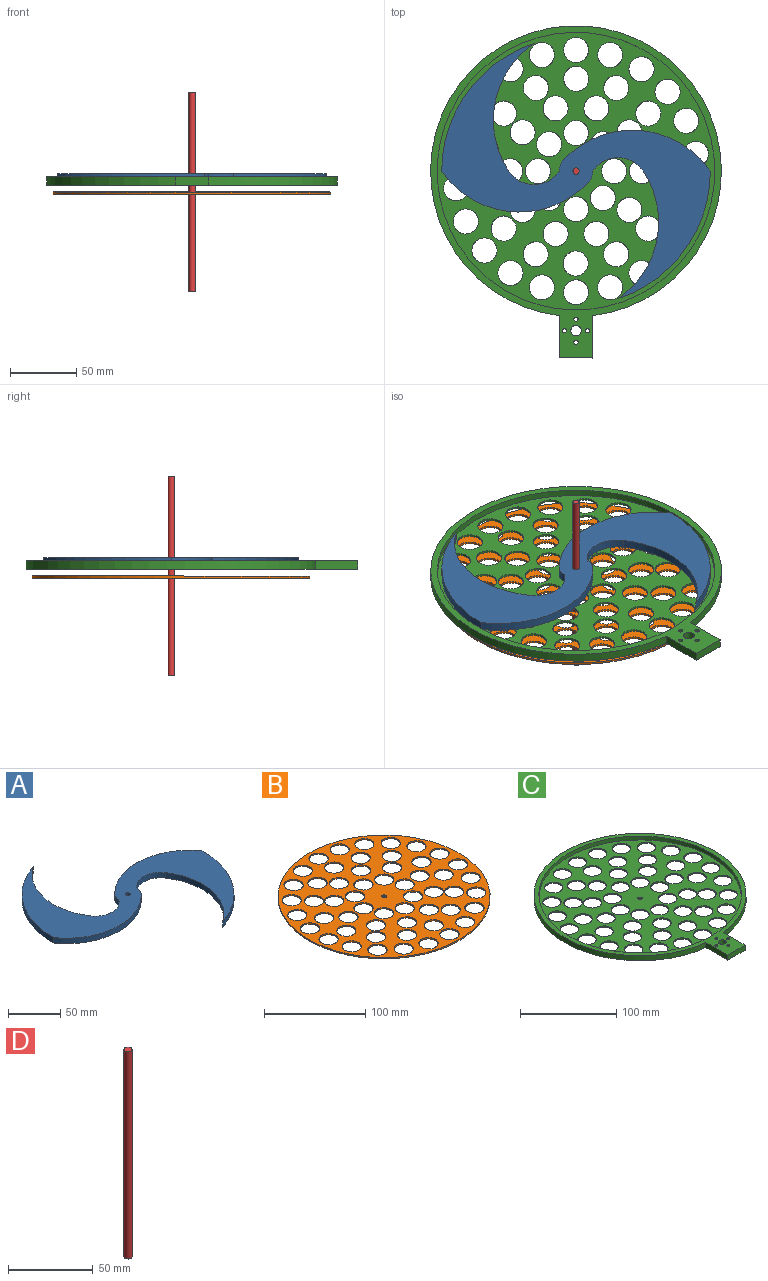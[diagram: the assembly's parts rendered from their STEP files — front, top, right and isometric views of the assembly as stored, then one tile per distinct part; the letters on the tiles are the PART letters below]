
ASSEMBLY  parts=4 mates=3
PART A: 13 faces, bbox 203.2x193x6.4 mm
  f0: cylinder r=22.9mm len=38.1mm, axis (0,0,-1), area 285.8mm2, adj f1,f10,f11,f12
  f1: cylinder r=69.74mm len=96.52mm, axis (0,0,-1), area 693.4mm2, adj f0,f2,f11,f12
  f2: cylinder r=101.6mm len=96.52mm, axis (0,0,-1), area 808.4mm2, adj f1,f3,f11,f12
  f3: cylinder r=71.61mm len=110.79mm, axis (0,0,-1), area 807.8mm2, adj f2,f4,f11,f12
  f4: cylinder r=12.7mm len=8.76mm, axis (0,0,-1), area 61.4mm2, adj f3,f5,f11,f12
  f5: cylinder r=22.9mm len=38.1mm, axis (0,0,-1), area 285.8mm2, adj f4,f6,f11,f12
  f6: cylinder r=69.74mm len=96.52mm, axis (0,0,-1), area 693.4mm2, adj f5,f7,f11,f12
  f7: cylinder r=101.6mm len=96.52mm, axis (0,0,-1), area 808.4mm2, adj f6,f8,f11,f12
  f8: cylinder r=71.6mm len=110.79mm, axis (0,0,-1), area 807.9mm2, adj f7,f10,f11,f12
  f9: cylinder r=2.38mm len=6.35mm, axis (0,0,-1), area 95mm2, adj f11,f12
  f10: cylinder r=12.7mm len=8.76mm, axis (0,0,-1), area 61.4mm2, adj f0,f8,f11,f12
  f11: plane 203.2x193.04mm, normal (0,0,1), area 9819.9mm2, adj f0,f1,f2,f3,f4,f5,f6,f7
  f12: plane 203.2x193.04mm, normal (0,0,-1), area 9819.9mm2, adj f0,f1,f2,f3,f4,f5,f6,f7
PART B: 58 faces, bbox 210x210x1.5 mm
  f0: cylinder r=9.53mm len=19.05mm, axis (0,0,-1), area 90.9mm2, adj f56,f57
  f1: cylinder r=9.53mm len=19.05mm, axis (0,0,-1), area 90.9mm2, adj f56,f57
  f2: cylinder r=9.53mm len=19.05mm, axis (0,0,-1), area 90.9mm2, adj f56,f57
  f3: cylinder r=9.53mm len=19.05mm, axis (0,0,-1), area 90.9mm2, adj f56,f57
  f4: cylinder r=9.53mm len=19.05mm, axis (0,0,-1), area 90.9mm2, adj f56,f57
  f5: cylinder r=9.53mm len=19.05mm, axis (0,0,-1), area 90.9mm2, adj f56,f57
  f6: cylinder r=9.53mm len=19.05mm, axis (0,0,-1), area 90.9mm2, adj f56,f57
  f7: cylinder r=9.53mm len=19.05mm, axis (0,0,-1), area 90.9mm2, adj f56,f57
  f8: cylinder r=9.53mm len=19.05mm, axis (0,0,-1), area 90.9mm2, adj f56,f57
  f9: cylinder r=9.53mm len=19.05mm, axis (0,0,-1), area 90.9mm2, adj f56,f57
  f10: cylinder r=9.53mm len=19.05mm, axis (0,0,-1), area 90.9mm2, adj f56,f57
  f11: cylinder r=9.53mm len=19.05mm, axis (0,0,-1), area 90.9mm2, adj f56,f57
  f12: cylinder r=9.53mm len=19.05mm, axis (0,0,-1), area 90.9mm2, adj f56,f57
  f13: cylinder r=9.53mm len=19.05mm, axis (0,0,-1), area 90.9mm2, adj f56,f57
  f14: cylinder r=9.53mm len=19.05mm, axis (0,0,-1), area 90.9mm2, adj f56,f57
  f15: cylinder r=9.53mm len=19.05mm, axis (0,0,-1), area 90.9mm2, adj f56,f57
  f16: cylinder r=9.53mm len=19.05mm, axis (0,0,-1), area 90.9mm2, adj f56,f57
  f17: cylinder r=9.53mm len=19.05mm, axis (0,0,-1), area 90.9mm2, adj f56,f57
  f18: cylinder r=9.53mm len=19.05mm, axis (0,0,-1), area 90.9mm2, adj f56,f57
  f19: cylinder r=9.53mm len=19.05mm, axis (0,0,-1), area 90.9mm2, adj f56,f57
  f20: cylinder r=9.53mm len=19.05mm, axis (0,0,-1), area 90.9mm2, adj f56,f57
  f21: cylinder r=9.53mm len=19.05mm, axis (0,0,-1), area 90.9mm2, adj f56,f57
  f22: cylinder r=9.53mm len=19.05mm, axis (0,0,-1), area 90.9mm2, adj f56,f57
  f23: cylinder r=9.53mm len=19.05mm, axis (0,0,-1), area 90.9mm2, adj f56,f57
  f24: cylinder r=9.53mm len=19.05mm, axis (0,0,-1), area 90.9mm2, adj f56,f57
  f25: cylinder r=9.53mm len=19.05mm, axis (0,0,-1), area 90.9mm2, adj f56,f57
  f26: cylinder r=9.53mm len=19.05mm, axis (0,0,-1), area 90.9mm2, adj f56,f57
  f27: cylinder r=9.53mm len=19.05mm, axis (0,0,-1), area 90.9mm2, adj f56,f57
  f28: cylinder r=9.53mm len=19.05mm, axis (0,0,-1), area 90.9mm2, adj f56,f57
  f29: cylinder r=9.53mm len=19.05mm, axis (0,0,-1), area 90.9mm2, adj f56,f57
  f30: cylinder r=9.53mm len=19.05mm, axis (0,0,-1), area 90.9mm2, adj f56,f57
  f31: cylinder r=9.53mm len=19.05mm, axis (0,0,-1), area 90.9mm2, adj f56,f57
  f32: cylinder r=9.53mm len=19.05mm, axis (0,0,-1), area 90.9mm2, adj f56,f57
  f33: cylinder r=9.53mm len=19.05mm, axis (0,0,-1), area 90.9mm2, adj f56,f57
  f34: cylinder r=2.38mm len=4.76mm, axis (0,0,-1), area 22.7mm2, adj f56,f57
  f35: cylinder r=9.53mm len=19.05mm, axis (0,0,-1), area 90.9mm2, adj f56,f57
  f36: cylinder r=9.53mm len=19.05mm, axis (0,0,-1), area 90.9mm2, adj f56,f57
  f37: cylinder r=9.53mm len=19.05mm, axis (0,0,-1), area 90.9mm2, adj f56,f57
  f38: cylinder r=9.53mm len=19.05mm, axis (0,0,-1), area 90.9mm2, adj f56,f57
  f39: cylinder r=9.53mm len=19.05mm, axis (0,0,-1), area 90.9mm2, adj f56,f57
  f40: cylinder r=9.53mm len=19.05mm, axis (0,0,-1), area 90.9mm2, adj f56,f57
  f41: cylinder r=9.53mm len=19.05mm, axis (0,0,-1), area 90.9mm2, adj f56,f57
  f42: cylinder r=9.53mm len=19.05mm, axis (0,0,-1), area 90.9mm2, adj f56,f57
  f43: cylinder r=9.53mm len=19.05mm, axis (0,0,-1), area 90.9mm2, adj f56,f57
  f44: cylinder r=9.53mm len=19.05mm, axis (0,0,-1), area 90.9mm2, adj f56,f57
  f45: cylinder r=9.53mm len=19.05mm, axis (0,0,-1), area 90.9mm2, adj f56,f57
  f46: cylinder r=9.53mm len=19.05mm, axis (0,0,-1), area 90.9mm2, adj f56,f57
  f47: cylinder r=9.53mm len=19.05mm, axis (0,0,-1), area 90.9mm2, adj f56,f57
  f48: cylinder r=9.53mm len=19.05mm, axis (0,0,-1), area 90.9mm2, adj f56,f57
  f49: cylinder r=9.53mm len=19.05mm, axis (0,0,-1), area 90.9mm2, adj f56,f57
  f50: cylinder r=9.53mm len=19.05mm, axis (0,0,-1), area 90.9mm2, adj f56,f57
  f51: cylinder r=9.53mm len=19.05mm, axis (0,0,-1), area 90.9mm2, adj f56,f57
  f52: cylinder r=9.53mm len=19.05mm, axis (0,0,-1), area 90.9mm2, adj f56,f57
  f53: cylinder r=9.53mm len=19.05mm, axis (0,0,-1), area 90.9mm2, adj f56,f57
  f54: cylinder r=9.53mm len=19.05mm, axis (0,0,-1), area 90.9mm2, adj f56,f57
  f55: cylinder r=105mm len=210mm, axis (0,0,-1), area 1002.1mm2, adj f56,f57
  f56: plane 210x210mm, normal (0,0,1), area 19227mm2, adj f0,f1,f2,f3,f4,f5,f6,f7
  f57: plane 210x210mm, normal (0,0,-1), area 19227mm2, adj f0,f1,f2,f3,f4,f5,f6,f7
PART C: 68 faces, bbox 220x251.3x6.4 mm
  f0: cylinder r=9.53mm len=19.05mm, axis (0,0,-1), area 90.9mm2, adj f55,f56
  f1: cylinder r=9.53mm len=19.05mm, axis (0,0,-1), area 90.9mm2, adj f55,f56
  f2: cylinder r=2.38mm len=4.76mm, axis (0,0,-1), area 22.7mm2, adj f55,f56
  f3: cylinder r=9.53mm len=19.05mm, axis (0,0,-1), area 90.9mm2, adj f55,f56
  f4: cylinder r=9.53mm len=19.05mm, axis (0,0,-1), area 90.9mm2, adj f55,f56
  f5: cylinder r=9.53mm len=19.05mm, axis (0,0,-1), area 90.9mm2, adj f55,f56
  f6: cylinder r=9.53mm len=19.05mm, axis (0,0,-1), area 90.9mm2, adj f55,f56
  f7: cylinder r=9.53mm len=19.05mm, axis (0,0,-1), area 90.9mm2, adj f55,f56
  f8: cylinder r=9.53mm len=19.05mm, axis (0,0,-1), area 90.9mm2, adj f55,f56
  f9: cylinder r=9.53mm len=19.05mm, axis (0,0,-1), area 90.9mm2, adj f55,f56
  f10: cylinder r=9.53mm len=19.05mm, axis (0,0,-1), area 90.9mm2, adj f55,f56
  f11: cylinder r=9.53mm len=19.05mm, axis (0,0,-1), area 90.9mm2, adj f55,f56
  f12: cylinder r=9.53mm len=19.05mm, axis (0,0,-1), area 90.9mm2, adj f55,f56
  f13: cylinder r=9.53mm len=19.05mm, axis (0,0,-1), area 90.9mm2, adj f55,f56
  f14: cylinder r=9.53mm len=19.05mm, axis (0,0,-1), area 90.9mm2, adj f55,f56
  f15: cylinder r=9.53mm len=19.05mm, axis (0,0,-1), area 90.9mm2, adj f55,f56
  f16: cylinder r=9.53mm len=19.05mm, axis (0,0,-1), area 90.9mm2, adj f55,f56
  f17: cylinder r=9.53mm len=19.05mm, axis (0,0,-1), area 90.9mm2, adj f55,f56
  f18: cylinder r=9.53mm len=19.05mm, axis (0,0,-1), area 90.9mm2, adj f55,f56
  f19: cylinder r=9.53mm len=19.05mm, axis (0,0,-1), area 90.9mm2, adj f55,f56
  f20: cylinder r=9.53mm len=19.05mm, axis (0,0,-1), area 90.9mm2, adj f55,f56
  f21: cylinder r=9.53mm len=19.05mm, axis (0,0,-1), area 90.9mm2, adj f55,f56
  f22: cylinder r=9.53mm len=19.05mm, axis (0,0,-1), area 90.9mm2, adj f55,f56
  f23: cylinder r=9.53mm len=19.05mm, axis (0,0,-1), area 90.9mm2, adj f55,f56
  f24: cylinder r=9.53mm len=19.05mm, axis (0,0,-1), area 90.9mm2, adj f55,f56
  f25: cylinder r=9.53mm len=19.05mm, axis (0,0,-1), area 90.9mm2, adj f55,f56
  f26: cylinder r=9.53mm len=19.05mm, axis (0,0,-1), area 90.9mm2, adj f55,f56
  f27: cylinder r=9.53mm len=19.05mm, axis (0,0,-1), area 90.9mm2, adj f55,f56
  f28: cylinder r=9.53mm len=19.05mm, axis (0,0,-1), area 90.9mm2, adj f55,f56
  f29: cylinder r=9.53mm len=19.05mm, axis (0,0,-1), area 90.9mm2, adj f55,f56
  f30: cylinder r=9.53mm len=19.05mm, axis (0,0,-1), area 90.9mm2, adj f55,f56
  f31: cylinder r=9.53mm len=19.05mm, axis (0,0,-1), area 90.9mm2, adj f55,f56
  f32: cylinder r=9.53mm len=19.05mm, axis (0,0,-1), area 90.9mm2, adj f55,f56
  f33: cylinder r=9.53mm len=19.05mm, axis (0,0,-1), area 90.9mm2, adj f55,f56
  f34: cylinder r=9.53mm len=19.05mm, axis (0,0,-1), area 90.9mm2, adj f55,f56
  f35: cylinder r=9.53mm len=19.05mm, axis (0,0,-1), area 90.9mm2, adj f55,f56
  f36: cylinder r=9.53mm len=19.05mm, axis (0,0,-1), area 90.9mm2, adj f55,f56
  f37: cylinder r=9.53mm len=19.05mm, axis (0,0,-1), area 90.9mm2, adj f55,f56
  f38: cylinder r=9.53mm len=19.05mm, axis (0,0,-1), area 90.9mm2, adj f55,f56
  f39: cylinder r=9.53mm len=19.05mm, axis (0,0,-1), area 90.9mm2, adj f55,f56
  f40: cylinder r=9.53mm len=19.05mm, axis (0,0,-1), area 90.9mm2, adj f55,f56
  f41: cylinder r=9.53mm len=19.05mm, axis (0,0,-1), area 90.9mm2, adj f55,f56
  f42: cylinder r=9.53mm len=19.05mm, axis (0,0,-1), area 90.9mm2, adj f55,f56
  f43: cylinder r=9.53mm len=19.05mm, axis (0,0,-1), area 90.9mm2, adj f55,f56
  f44: cylinder r=9.53mm len=19.05mm, axis (0,0,-1), area 90.9mm2, adj f55,f56
  f45: cylinder r=9.53mm len=19.05mm, axis (0,0,-1), area 90.9mm2, adj f55,f56
  f46: cylinder r=9.53mm len=19.05mm, axis (0,0,-1), area 90.9mm2, adj f55,f56
  f47: cylinder r=9.53mm len=19.05mm, axis (0,0,-1), area 90.9mm2, adj f55,f56
  f48: cylinder r=9.53mm len=19.05mm, axis (0,0,-1), area 90.9mm2, adj f55,f56
  f49: cylinder r=9.53mm len=19.05mm, axis (0,0,-1), area 90.9mm2, adj f55,f56
  f50: cylinder r=9.53mm len=19.05mm, axis (0,0,-1), area 90.9mm2, adj f55,f56
  f51: cylinder r=9.53mm len=19.05mm, axis (0,0,-1), area 90.9mm2, adj f55,f56
  f52: cylinder r=9.53mm len=19.05mm, axis (0,0,-1), area 90.9mm2, adj f55,f56
  f53: cylinder r=9.53mm len=19.05mm, axis (0,0,-1), area 90.9mm2, adj f55,f56
  f54: cylinder r=9.53mm len=19.05mm, axis (0,0,-1), area 90.9mm2, adj f55,f56
  f55: plane 210x210mm, normal (0,0,1), area 19227mm2, adj f0,f1,f2,f3,f4,f5,f6,f7
  f56: plane 251.34x220mm, normal (0,0,-1), area 23325.3mm2, adj f0,f1,f2,f3,f4,f5,f6,f7
  f57: cylinder r=105mm len=210mm, axis (0,0,-1), area 3187.2mm2, adj f55,f67
  f58: cylinder r=110mm len=220mm, axis (0,0,-1), area 4227.2mm2, adj f56,f59,f65,f67
  f59: plane 32.07x6.35mm, normal (-1,0,0), area 203.7mm2, adj f56,f58,f60,f67
  f60: plane 25.4x6.35mm, normal (0,-1,0), area 161.3mm2, adj f56,f59,f65,f67
  f61: cylinder r=1.59mm len=6.35mm, axis (0,0,-1), area 63.3mm2, adj f56,f67
  f62: cylinder r=1.59mm len=6.35mm, axis (0,0,-1), area 63.3mm2, adj f56,f67
  f63: cylinder r=1.59mm len=6.35mm, axis (0,0,-1), area 63.3mm2, adj f56,f67
  f64: cylinder r=3.97mm len=7.94mm, axis (0,0,-1), area 158.3mm2, adj f56,f67
  f65: plane 32.07x6.35mm, normal (1,0,0), area 203.7mm2, adj f56,f58,f60,f67
  f66: cylinder r=1.59mm len=6.35mm, axis (0,0,-1), area 63.3mm2, adj f56,f67
  f67: plane 251.34x220mm, normal (0,0,1), area 4098.3mm2, adj f57,f58,f59,f60,f61,f62,f63,f64
PART D: 3 faces, bbox 4.8x4.8x150 mm
  f0: cylinder r=2.38mm len=150mm, axis (0,0,-1), area 2244.3mm2, adj f1,f2
  f1: plane 4.76x4.76mm, normal (0,0,1), area 17.8mm2, adj f0
  f2: plane 4.76x4.76mm, normal (0,0,-1), area 17.8mm2, adj f0
PLACE A rot(axis=(0.98,0.09,-0.15),0deg) t=(-88.39,-5.74,9.71)mm
PLACE B rot(axis=(0,0,1),180deg) t=(-88.39,-5.74,0.7)mm
PLACE C rot(axis=(0.98,0.09,-0.15),0deg) t=(-88.39,-5.74,7.39)mm
PLACE D rot(axis=(0.98,0.09,-0.15),0deg) t=(-88.39,-5.74,2.21)mm
MATE cylindrical C.f2 <-> D.f0  axis (0,0,1) through (-88.39,-5.74,8.91)mm
MATE revolute B.f34 <-> D.f0  axis (0,0,1) through (-88.39,-5.74,2.21)mm
MATE cylindrical A.f4 <-> D.f0  axis (0,0,1) through (-88.39,-5.74,16.06)mm
